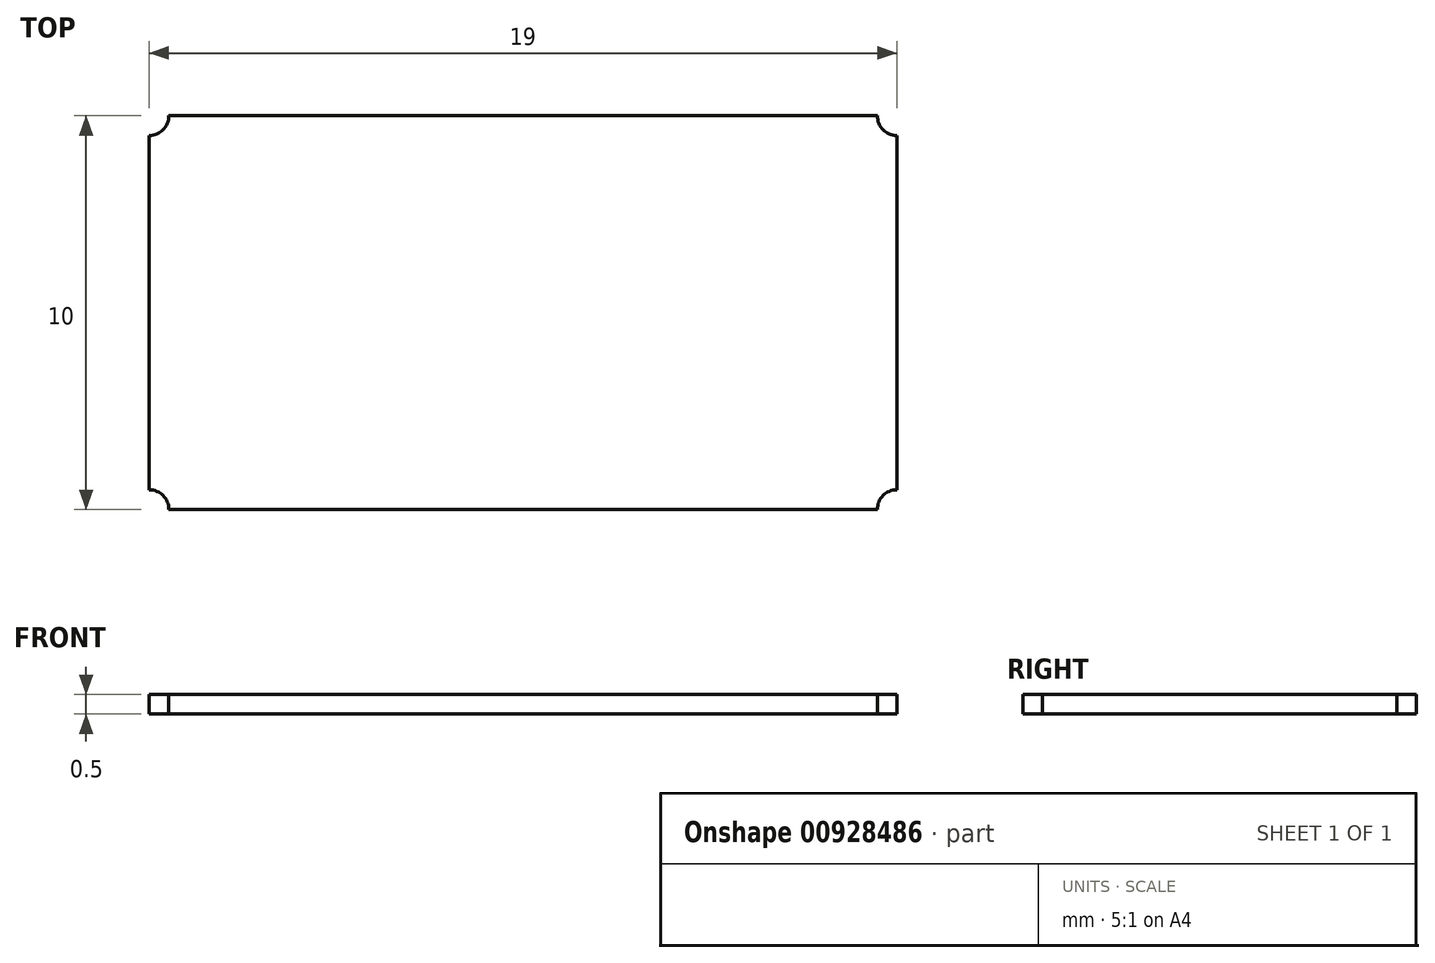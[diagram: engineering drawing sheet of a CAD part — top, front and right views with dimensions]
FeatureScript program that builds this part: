
annotation { "Feature Type Name" : "Feature", "Feature Type Description" : "" }
export const myFeature = defineFeature(function(context is Context, id is Id, definition is map)
    precondition{}
    {
        {
            var Q0;
            Q0=qCreatedBy(makeId("Top.planeOp"),FACE);
            var sketch = newSketch(context, id + "F0", { "sketchPlane" : qUnion([Q0])});
            skLineSegment(sketch, "E0.bottom", {"start": v(9, 5) * mm, "end": v(-9, 5) * mm});
            skLineSegment(sketch, "E0.top", {"start": v(9, -5) * mm, "end": v(-9, -5) * mm});
            skLineSegment(sketch, "E0.left", {"start": v(9.5, 4.5) * mm, "end": v(9.5, -4.5) * mm});
            skLineSegment(sketch, "E0.right", {"start": v(-9.5, 4.5) * mm, "end": v(-9.5, -4.5) * mm});
            skPoint(sketch, "E0.middle", {"position": v(0, 0) * mm});
            skArc(sketch, "E1", {"start": v(9, 5) * mm, "mid": v(9.15, 4.65) * mm, "end": v(9.5, 4.5) * mm});
            skArc(sketch, "E2", {"start": v(9.5, -4.5) * mm, "mid": v(9.15, -4.65) * mm, "end": v(9, -5) * mm});
            skArc(sketch, "E3", {"start": v(-9.5, 4.5) * mm, "mid": v(-9.15, 4.65) * mm, "end": v(-9, 5) * mm});
            skArc(sketch, "E4", {"start": v(-9, -5) * mm, "mid": v(-9.15, -4.65) * mm, "end": v(-9.5, -4.5) * mm});
            skSolve(sketch);
        }
        {
            var Q0;
            Q0=makeQuery(id+"F0.imprint","IMPRINT",FACE,{"disambiguationData":[TD([[makeQuery(id+"F0.imprint","IMPRINT",EDGE,{"derivedFrom":sQuery(id+"F0.wireOp",EDGE,"E0.bottom")}),1.0]])]});
            extrude(context, id + "F1", {"entities" : qUnion([Q0]), "depth" : 0.5 * mm, "offsetDistance" : 25 * mm});
        }
    });
